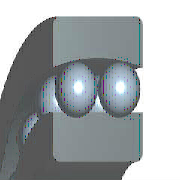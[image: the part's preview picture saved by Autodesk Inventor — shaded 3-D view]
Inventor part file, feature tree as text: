
AUTODESK INVENTOR PART (.ipt)
format: ipt  version: 2022.1 (Build 261234000, 234)  size: 389,632 bytes
history: native  units: mm (DEFAULTED — no unit token found)
features: other x3, sketch x1, pattern_circular x1, pattern_linear x1
ambient origin geometry x8: Origin, YZ Plane, XZ Plane, XY Plane, X Axis, Y Axis, Z Axis, Center Point
bodies: Solid1 (feature_tree)
feature tree (6):
  sketch  "Boceto1"  dims[d19=90.0deg d0=1.0mm d1=180.0deg d2=120.0mm d3=360.0deg d4=6.08mm d5=0.0mm d6=0.0mm d7=0.0mm d8=30.0mm d9=62.0mm d10=20.0mm d11=6.306667mm d12=40.432mm d13=46.0mm d14=0.0mm d15=0.0mm d16=180.0deg d17=20.0mm d18=-7.386667mm]
  other  "Cuerpo"
  other  "Bola1"
  other  "Bola2"
  pattern_circular  "Bolas1"  [2 undecoded]
  pattern_linear  "Bolas2"  Spacing1=180.0deg  [1 undecoded]
note: 3 required parameter values undecoded (feature->parameter linkage not recoverable at this tier; creation-order binding heuristic only, values carry confidence <= 0.55)
